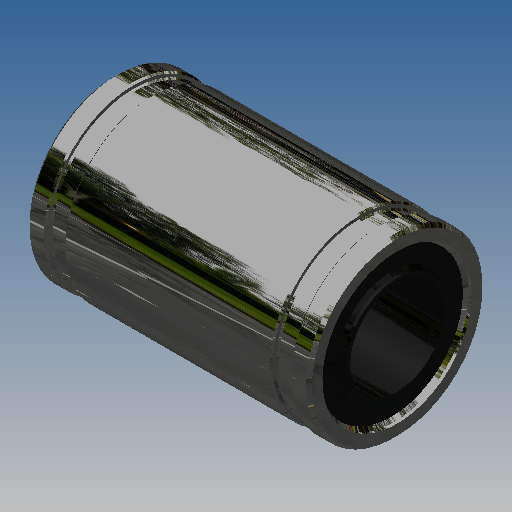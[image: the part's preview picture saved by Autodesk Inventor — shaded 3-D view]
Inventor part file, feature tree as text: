
AUTODESK INVENTOR PART (.ipt)
format: ipt  version: 2018 (Build 220112000, 112)  size: 333,824 bytes
history: native  units: in
note: dims shown in document units (in); Inventor stores cm internally (conversion verified against a paired STEP export)
features: chamfer x2, revolve x1, sketch x1
ambient origin geometry x8: Origin, YZ Plane, XZ Plane, XY Plane, X Axis, Y Axis, Z Axis, Center Point
bodies: Solid1 (feature_tree)
feature tree (4):
  revolve  "Revolution1"  [1 undecoded]
  chamfer  "Chamfer1"  Distance=0.2953in
  chamfer  "Chamfer2"  Distance=0.02in
  sketch  "Sketch1"  dims[d0=0.9252in d1=0.1575in d2=0.2953in d3=0.02in d4=0.9449in d5=0.9449in d6=0.063in d7=0.063in d8=90.0deg d9=0.01in d10=0.125in d11=45.0deg d12=0.005in d13=0.125in d14=45.0deg]
note: 1 required parameter value undecoded (feature->parameter linkage not recoverable at this tier; creation-order binding heuristic only, values carry confidence <= 0.55)
